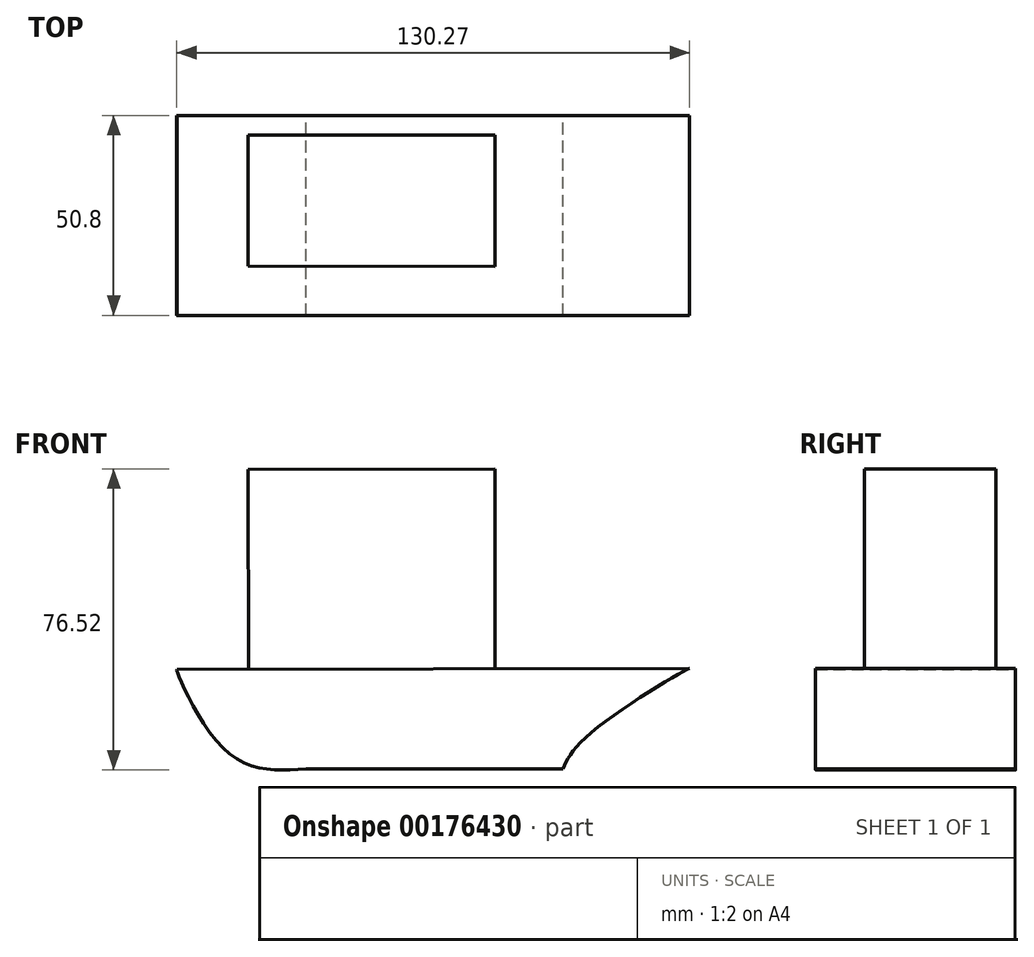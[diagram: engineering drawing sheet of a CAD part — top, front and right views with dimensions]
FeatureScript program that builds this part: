
annotation { "Feature Type Name" : "Feature", "Feature Type Description" : "" }
export const myFeature = defineFeature(function(context is Context, id is Id, definition is map)
    precondition{}
    {
        {
            var Q0;
            Q0=qCreatedBy(makeId("Front.planeOp"),FACE);
            var sketch = newSketch(context, id + "F0", { "sketchPlane" : qUnion([Q0])});
            skLineSegment(sketch, "E0", {"start": v(-29.78, -30.08) * mm, "end": v(35.5, -30.08) * mm});
            skFitSpline(sketch, "E1", {"points": [v(35.5, -30.08) * mm, v(42.11, -21.36) * mm, v(67.68, -4.51) * mm, v(67.98, -4.51) * mm], "startDerivative": vector(9.62, 21.08) * mm, "endDerivative": vector(2.74, -1.57) * mm});
            skFitSpline(sketch, "E2", {"points": [v(-29.78, -30.08) * mm, v(-49.93, -25.57) * mm, v(-62.56, -5.11) * mm, v(-62.56, -4.81) * mm], "startDerivative": vector(-46.23, -3.16) * mm, "endDerivative": vector(1.2, 2.95) * mm});
            skLineSegment(sketch, "E3", {"start": v(-62.56, -4.81) * mm, "end": v(67.98, -4.51) * mm});
            skSolve(sketch);
        }
        {
            var Q0;
            {var subQ0=sQuery(id+"F0.wireOp",EDGE,"E0");Q0=makeQuery(id+"F0.imprint","IMPRINT",FACE,{"disambiguationData":[TD([[makeQuery(id+"F0.imprint","IMPRINT",EDGE,{"derivedFrom":subQ0}),1.0]])]});}
            extrude(context, id + "F1", {"entities" : qUnion([Q0]), "depth" : 50.8 * mm});
        }
        {
            var Q0;
            Q0=makeQuery(id+"F1.opExtrude","SWEPT_FACE",FACE,{"disambiguationData":[OSD([sQuery(id+"F0.wireOp",EDGE,"E3")])]});
            var sketch = newSketch(context, id + "F2", { "sketchPlane" : qUnion([Q0])});
            skLineSegment(sketch, "E4", {"start": v(44.15, -32.82) * mm, "end": v(44.15, -13.2) * mm});
            skLineSegment(sketch, "E5", {"start": v(44.15, -13.2) * mm, "end": v(31.2, -13.2) * mm});
            skLineSegment(sketch, "E6", {"start": v(31.2, -13.2) * mm, "end": v(31.2, -30.74) * mm});
            skLineSegment(sketch, "E7", {"start": v(31.2, -30.74) * mm, "end": v(44.15, -32.82) * mm});
            skLineSegment(sketch, "E8", {"start": v(18.3, -38.38) * mm, "end": v(18.3, -4.96) * mm});
            skLineSegment(sketch, "E9", {"start": v(18.3, -4.96) * mm, "end": v(-44.36, -4.96) * mm});
            skLineSegment(sketch, "E10", {"start": v(-44.36, -4.96) * mm, "end": v(-44.36, -38.28) * mm});
            skLineSegment(sketch, "E11", {"start": v(-44.36, -38.28) * mm, "end": v(18.3, -38.38) * mm});
            skSolve(sketch);
        }
        {
            var Q0;
            Q0=makeQuery(id+"F2.imprint","IMPRINT",FACE,{"disambiguationData":[TD([[makeQuery(id+"F2.imprint","IMPRINT",EDGE,{"derivedFrom":sQuery(id+"F2.wireOp",EDGE,"E8")}),1.0]])]});
            extrude(context, id + "F3", {"entities" : qUnion([Q0]), "operationType" : NewBodyOperationType.ADD, "depth" : 50.8 * mm});
        }
    });
